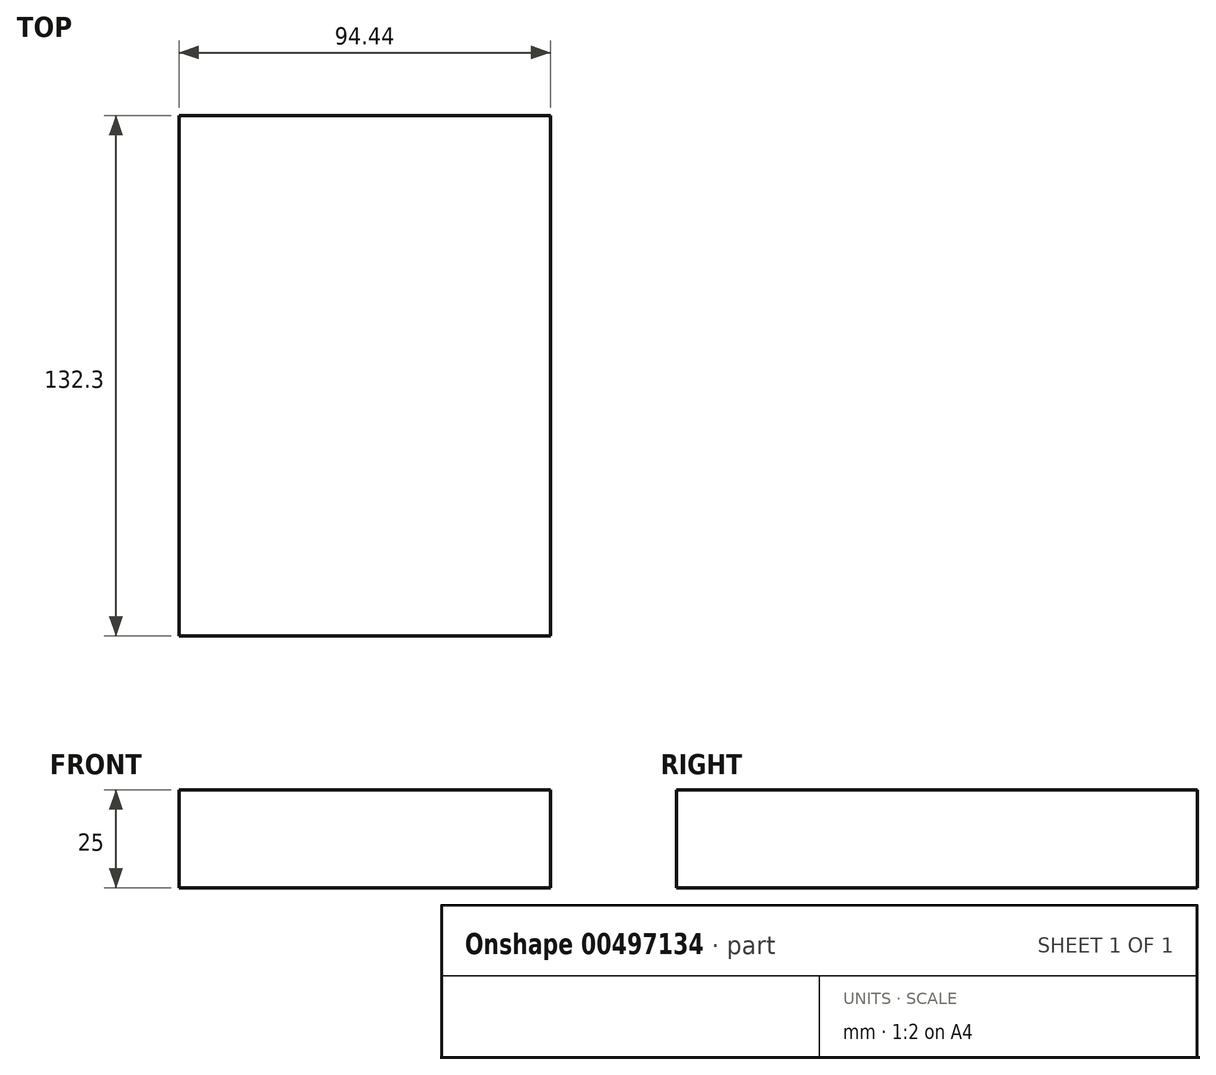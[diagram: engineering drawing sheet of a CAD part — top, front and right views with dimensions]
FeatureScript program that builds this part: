
annotation { "Feature Type Name" : "Feature", "Feature Type Description" : "" }
export const myFeature = defineFeature(function(context is Context, id is Id, definition is map)
    precondition{}
    {
        {
            var Q0;
            Q0=qCreatedBy(makeId("Top.planeOp"),FACE);
            var sketch = newSketch(context, id + "F0", { "sketchPlane" : qUnion([Q0])});
            skLineSegment(sketch, "E0.bottom", {"start": v(27.97, 90.6) * mm, "end": v(-66.47, 90.6) * mm});
            skLineSegment(sketch, "E0.top", {"start": v(27.97, -41.71) * mm, "end": v(-66.47, -41.71) * mm});
            skLineSegment(sketch, "E0.left", {"start": v(27.97, 90.6) * mm, "end": v(27.97, -41.71) * mm});
            skLineSegment(sketch, "E0.right", {"start": v(-66.47, 90.6) * mm, "end": v(-66.47, -41.71) * mm});
            skSolve(sketch);
        }
        {
            var Q0;
            Q0 = qSketchRegion(id + "F0", true);
            var Q1;
            Q1=makeQuery(id+"F0.imprint","IMPRINT",FACE,{"disambiguationData":[TD([[makeQuery(id+"F0.imprint","IMPRINT",EDGE,{"derivedFrom":sQuery(id+"F0.wireOp",EDGE,"E0.bottom")}),1.0]])]});
            extrude(context, id + "F1", {"entities" : qUnion([Q0, Q1]), "depth" : 25 * mm});
        }
    });
